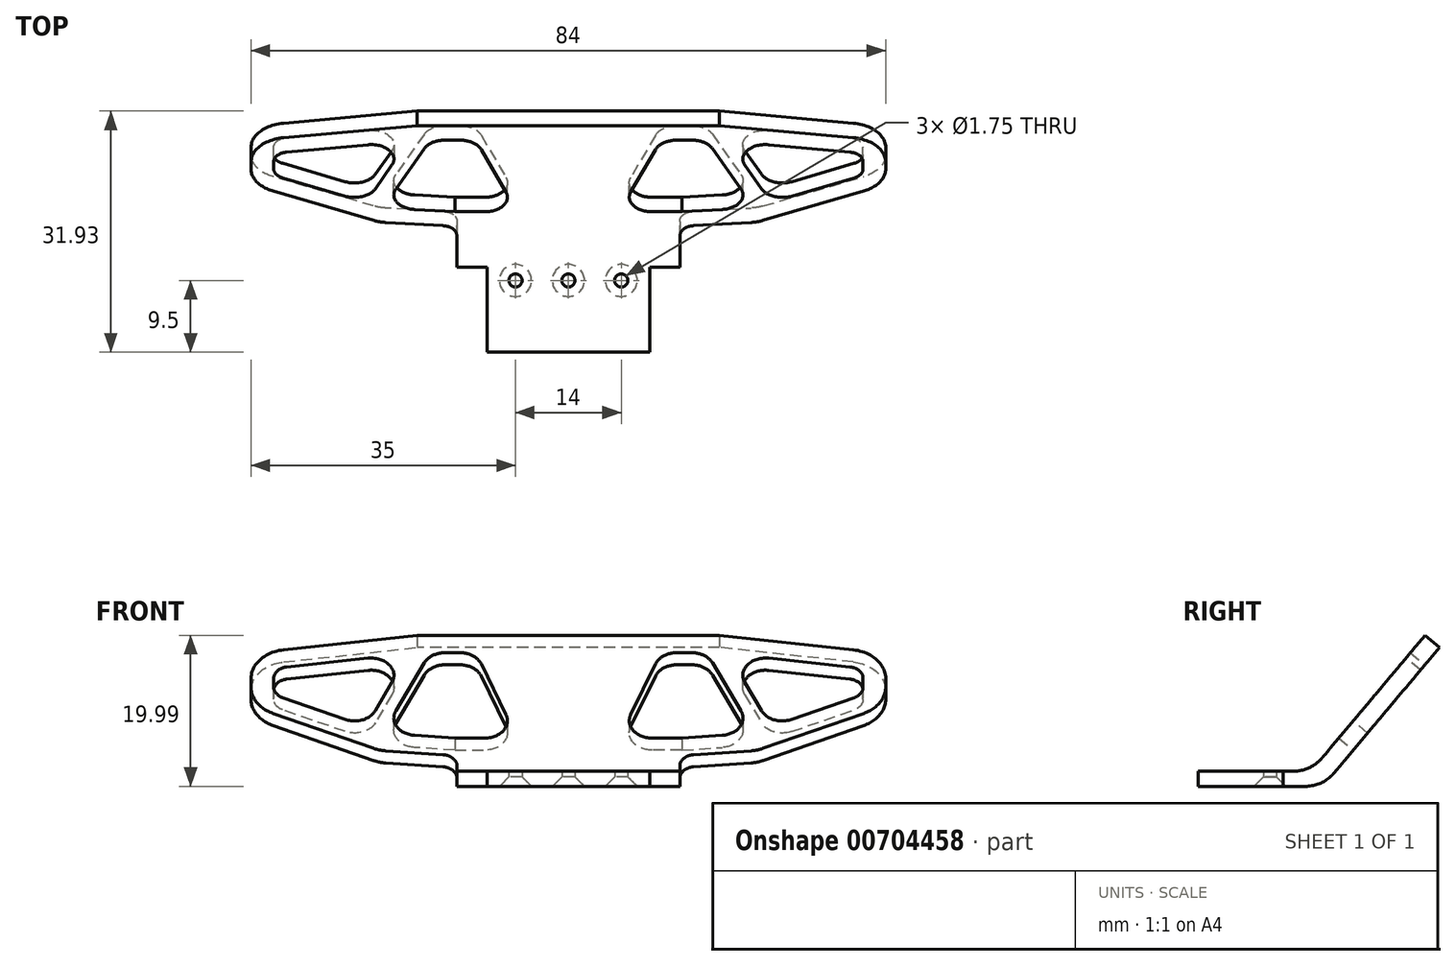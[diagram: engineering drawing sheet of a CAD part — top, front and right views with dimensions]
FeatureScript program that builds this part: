
annotation { "Feature Type Name" : "Feature", "Feature Type Description" : "" }
export const myFeature = defineFeature(function(context is Context, id is Id, definition is map)
    precondition{}
    {
        {
            var Q0;
            Q0=qCreatedBy(makeId("Top.planeOp"),FACE);
            var sketch = newSketch(context, id + "F0", { "sketchPlane" : qUnion([Q0])});
            skLineSegment(sketch, "E0", {"start": v(0, 0) * mm, "end": v(0, -25.33) * mm, "construction": true});
            skCircle(sketch, "E1", {"center": v(0, -7) * mm, "radius": 0.87 * mm});
            skCircle(sketch, "E2", {"center": v(-7, -7) * mm, "radius": 0.88 * mm});
            skLineSegment(sketch, "E3", {"start": v(0, 0) * mm, "end": v(-14.75, 0) * mm});
            skLineSegment(sketch, "E4", {"start": v(-10.75, -5.25) * mm, "end": v(-10.75, -16.5) * mm});
            skLineSegment(sketch, "E5", {"start": v(-10.75, -16.5) * mm, "end": v(0, -16.5) * mm});
            skLineSegment(sketch, "E6", {"start": v(-10.75, -5.25) * mm, "end": v(-14.75, -5.25) * mm});
            skLineSegment(sketch, "E7", {"start": v(-14.75, -5.25) * mm, "end": v(-14.75, 0) * mm});
            skLineSegment(sketch, "E8", {"start": v(-14.75, -2) * mm, "end": v(0, -2) * mm, "construction": true});
            skLineSegment(sketch, "E9.MirrorCS", {"start": v(0, 0) * mm, "end": v(14.75, 0) * mm});
            skLineSegment(sketch, "E10.MirrorCS", {"start": v(14.75, -5.25) * mm, "end": v(14.75, 0) * mm});
            skLineSegment(sketch, "E11.MirrorCS", {"start": v(10.75, -5.25) * mm, "end": v(14.75, -5.25) * mm});
            skLineSegment(sketch, "E12.MirrorCS", {"start": v(10.75, -5.25) * mm, "end": v(10.75, -16.5) * mm});
            skLineSegment(sketch, "E13.MirrorCS", {"start": v(10.75, -16.5) * mm, "end": v(0, -16.5) * mm});
            skCircle(sketch, "E14.MirrorC", {"center": v(7, -7) * mm, "radius": 0.88 * mm});
            skLineSegment(sketch, "E15", {"start": v(-14.75, 5) * mm, "end": v(14.75, 5) * mm, "construction": true});
            skSolve(sketch);
        }
        {
            var Q0;
            Q0=makeQuery(id+"F0.imprint","IMPRINT",FACE,{"disambiguationData":[TD([[makeQuery(id+"F0.imprint","IMPRINT",EDGE,{"derivedFrom":sQuery(id+"F0.wireOp",EDGE,"E1")}),-1.0]])]});
            extrude(context, id + "F1", {"entities" : qUnion([Q0]), "depth" : 2 * mm, "offsetDistance" : 25 * mm});
        }
        {
            var Q0;
            Q0=makeQuery(id+"F1.opExtrude","CAP_EDGE",EDGE,{"disambiguationData":[OSD([sQuery(id+"F0.wireOp",EDGE,"E3"),sQuery(id+"F0.wireOp",EDGE,"E9.MirrorCS")])],"isStart":true});
            cPlane(context, id + "F2", {"entities" : qUnion([Q0]), "cplaneType" : CPlaneType.LINE_ANGLE, "offset" : 25 * mm, "angle" : 40 * degree, "oppositeDirection" : true, "width" : 150 * mm, "height" : 150 * mm});
        }
        {
            var Q0;
            Q0=qCreatedBy(id+"F2.planeOp",FACE);
            var sketch = newSketch(context, id + "F3", { "sketchPlane" : qUnion([Q0])});
            skLineSegment(sketch, "E16.0", {"start": v(14.75, 0) * mm, "end": v(-14.75, 0) * mm});
            skLineSegment(sketch, "E17", {"start": v(0, 0) * mm, "end": v(0, 3.21) * mm, "construction": true});
            skLineSegment(sketch, "E18.0", {"start": v(14.75, 3.21) * mm, "end": v(-14.75, 3.21) * mm, "construction": true});
            skLineSegment(sketch, "E19", {"start": v(0, 24) * mm, "end": v(-20, 24) * mm});
            skLineSegment(sketch, "E20", {"start": v(-16.58, 3.37) * mm, "end": v(-24.15, 4.04) * mm});
            skLineSegment(sketch, "E21", {"start": v(-14.75, 0) * mm, "end": v(-14.75, 1.38) * mm});
            skPoint(sketch, "E22.visualSharp", {"position": v(-14.75, 3.21) * mm});
            skArc(sketch, "E22.filletArc", {"start": v(-14.75, 1.38) * mm, "mid": v(-15.28, 2.73) * mm, "end": v(-16.58, 3.37) * mm});
            skLineSegment(sketch, "E23", {"start": v(-25.78, 4.46) * mm, "end": v(-39.07, 10.5) * mm});
            skPoint(sketch, "E24.visualSharp", {"position": v(-25, 4.11) * mm});
            skArc(sketch, "E24.filletArc", {"start": v(-25.78, 4.46) * mm, "mid": v(-24.98, 4.18) * mm, "end": v(-24.15, 4.04) * mm});
            skLineSegment(sketch, "E25", {"start": v(-42, 15.05) * mm, "end": v(-42, 16.55) * mm});
            skLineSegment(sketch, "E26", {"start": v(-37.7, 21.5) * mm, "end": v(-20, 24) * mm});
            skPoint(sketch, "E27.visualSharp", {"position": v(-42, 20.9) * mm});
            skArc(sketch, "E27.filletArc", {"start": v(-37.7, 21.5) * mm, "mid": v(-40.77, 19.83) * mm, "end": v(-42, 16.55) * mm});
            skPoint(sketch, "E28.visualSharp", {"position": v(-42, 11.83) * mm});
            skArc(sketch, "E28.filletArc", {"start": v(-42, 15.05) * mm, "mid": v(-41.2, 12.34) * mm, "end": v(-39.07, 10.5) * mm});
            skLineSegment(sketch, "E29.MirrorCS", {"start": v(0, 24) * mm, "end": v(20, 24) * mm});
            skLineSegment(sketch, "E30.MirrorCS", {"start": v(37.7, 21.5) * mm, "end": v(20, 24) * mm});
            skArc(sketch, "E31.MirrorCS", {"start": v(37.7, 21.5) * mm, "mid": v(40.77, 19.83) * mm, "end": v(42, 16.55) * mm});
            skArc(sketch, "E32.MirrorCS", {"start": v(42, 15.05) * mm, "mid": v(41.2, 12.34) * mm, "end": v(39.07, 10.5) * mm});
            skLineSegment(sketch, "E33.MirrorCS", {"start": v(25.78, 4.46) * mm, "end": v(39.07, 10.5) * mm});
            skLineSegment(sketch, "E34.MirrorCS", {"start": v(16.58, 3.37) * mm, "end": v(24.15, 4.04) * mm});
            skArc(sketch, "E35.MirrorCS", {"start": v(14.75, 1.38) * mm, "mid": v(15.28, 2.73) * mm, "end": v(16.58, 3.37) * mm});
            skArc(sketch, "E36.MirrorCS", {"start": v(25.78, 4.46) * mm, "mid": v(24.98, 4.18) * mm, "end": v(24.15, 4.04) * mm});
            skLineSegment(sketch, "E37.MirrorCS", {"start": v(42, 15.05) * mm, "end": v(42, 16.55) * mm});
            skLineSegment(sketch, "E38", {"start": v(14.75, 1.38) * mm, "end": v(14.75, 0) * mm});
            skSolve(sketch);
        }
        {
            var Q0;
            Q0=makeQuery(id+"F3.imprint","IMPRINT",FACE,{"disambiguationData":[TD([[makeQuery(id+"F3.imprint","IMPRINT",EDGE,{"derivedFrom":sQuery(id+"F3.wireOp",EDGE,"E16.0")}),-1.0]])]});
            extrude(context, id + "F4", {"entities" : qUnion([Q0]), "operationType" : NewBodyOperationType.ADD, "oppositeDirection" : true, "depth" : 2.5 * mm, "offsetDistance" : 25 * mm});
        }
        {
            var Q0;
            Q0=makeQuery(id+"F4.opExtrude","CAP_FACE",FACE,{"disambiguationData":[OSD([sQuery(id+"F3.wireOp",EDGE,"E16.0"),sQuery(id+"F3.wireOp",EDGE,"E19"),sQuery(id+"F3.wireOp",EDGE,"E20"),sQuery(id+"F3.wireOp",EDGE,"E21"),sQuery(id+"F3.wireOp",EDGE,"E22.filletArc"),sQuery(id+"F3.wireOp",EDGE,"E23"),sQuery(id+"F3.wireOp",EDGE,"E24.filletArc"),sQuery(id+"F3.wireOp",EDGE,"E25"),sQuery(id+"F3.wireOp",EDGE,"E26"),sQuery(id+"F3.wireOp",EDGE,"E27.filletArc"),sQuery(id+"F3.wireOp",EDGE,"E28.filletArc"),sQuery(id+"F3.wireOp",EDGE,"E29.MirrorCS"),sQuery(id+"F3.wireOp",EDGE,"E30.MirrorCS"),sQuery(id+"F3.wireOp",EDGE,"E31.MirrorCS"),sQuery(id+"F3.wireOp",EDGE,"E32.MirrorCS"),sQuery(id+"F3.wireOp",EDGE,"E33.MirrorCS"),sQuery(id+"F3.wireOp",EDGE,"E34.MirrorCS"),sQuery(id+"F3.wireOp",EDGE,"E35.MirrorCS"),sQuery(id+"F3.wireOp",EDGE,"E36.MirrorCS"),sQuery(id+"F3.wireOp",EDGE,"E37.MirrorCS"),sQuery(id+"F3.wireOp",EDGE,"E38")])],"isStart":true});
            var sketch = newSketch(context, id + "F5", { "sketchPlane" : qUnion([Q0])});
            skLineSegment(sketch, "E39.0", {"start": v(-18.27, 21) * mm, "end": v(-12.27, 21) * mm});
            skLineSegment(sketch, "E39.1", {"start": v(-37.28, 18.53) * mm, "end": v(-21.1, 20.81) * mm});
            skArc(sketch, "E39.2", {"start": v(-37.28, 18.53) * mm, "mid": v(-38.5, 17.86) * mm, "end": v(-39, 16.55) * mm});
            skLineSegment(sketch, "E39.3", {"start": v(-39, 15.05) * mm, "end": v(-39, 16.55) * mm});
            skLineSegment(sketch, "E39.4", {"start": v(-15.03, 6.25) * mm, "end": v(-23.89, 7.02) * mm});
            skArc(sketch, "E39.5", {"start": v(-24.54, 7.2) * mm, "mid": v(-24.22, 7.08) * mm, "end": v(-23.89, 7.02) * mm});
            skLineSegment(sketch, "E39.6", {"start": v(-26.81, 8.23) * mm, "end": v(-37.83, 13.23) * mm});
            skArc(sketch, "E39.7", {"start": v(-39, 15.05) * mm, "mid": v(-38.68, 13.97) * mm, "end": v(-37.83, 13.23) * mm});
            skLineSegment(sketch, "E40", {"start": v(-21.1, 20.81) * mm, "end": v(-26.81, 8.23) * mm});
            skLineSegment(sketch, "E41.0", {"start": v(-18.27, 21) * mm, "end": v(-24.54, 7.2) * mm});
            skLineSegment(sketch, "E42", {"start": v(-15.03, 6.25) * mm, "end": v(-6.73, 6.25) * mm});
            skLineSegment(sketch, "E43", {"start": v(-12.27, 21) * mm, "end": v(-6.73, 6.25) * mm});
            skLineSegment(sketch, "E44.MirrorCS", {"start": v(12.27, 21) * mm, "end": v(6.73, 6.25) * mm});
            skLineSegment(sketch, "E45.MirrorCS", {"start": v(18.27, 21) * mm, "end": v(24.54, 7.2) * mm});
            skArc(sketch, "E46.MirrorCS", {"start": v(24.54, 7.2) * mm, "mid": v(24.22, 7.08) * mm, "end": v(23.89, 7.02) * mm});
            skLineSegment(sketch, "E47.MirrorCS", {"start": v(15.03, 6.25) * mm, "end": v(23.89, 7.02) * mm});
            skLineSegment(sketch, "E48.MirrorCS", {"start": v(15.03, 6.25) * mm, "end": v(6.73, 6.25) * mm});
            skLineSegment(sketch, "E49.MirrorCS", {"start": v(21.1, 20.81) * mm, "end": v(26.81, 8.23) * mm});
            skLineSegment(sketch, "E50.MirrorCS", {"start": v(37.28, 18.53) * mm, "end": v(21.1, 20.81) * mm});
            skLineSegment(sketch, "E51.MirrorCS", {"start": v(26.81, 8.23) * mm, "end": v(37.83, 13.23) * mm});
            skArc(sketch, "E52.MirrorCS", {"start": v(39, 15.05) * mm, "mid": v(38.68, 13.97) * mm, "end": v(37.83, 13.23) * mm});
            skLineSegment(sketch, "E53.MirrorCS", {"start": v(39, 15.05) * mm, "end": v(39, 16.55) * mm});
            skArc(sketch, "E54.MirrorCS", {"start": v(37.28, 18.53) * mm, "mid": v(38.5, 17.86) * mm, "end": v(39, 16.55) * mm});
            skLineSegment(sketch, "E55.trimOffspring", {"start": v(12.27, 21) * mm, "end": v(18.27, 21) * mm});
            skPoint(sketch, "E56.orphan", {"position": v(0, 6.25) * mm});
            skSolve(sketch);
        }
        {
            var Q0;
            Q0=makeQuery(id+"F5.imprint","IMPRINT",FACE,{"disambiguationData":[TD([[makeQuery(id+"F5.imprint","IMPRINT",EDGE,{"derivedFrom":sQuery(id+"F5.wireOp",EDGE,"E39.1")}),-1.0]])]});
            var Q1;
            Q1=makeQuery(id+"F5.imprint","IMPRINT",FACE,{"disambiguationData":[TD([[makeQuery(id+"F5.imprint","IMPRINT",EDGE,{"derivedFrom":sQuery(id+"F5.wireOp",EDGE,"E39.0")}),-1.0]])]});
            var Q2;
            Q2=makeQuery(id+"F5.imprint","IMPRINT",FACE,{"disambiguationData":[TD([[makeQuery(id+"F5.imprint","IMPRINT",EDGE,{"derivedFrom":sQuery(id+"F5.wireOp",EDGE,"E44.MirrorCS")}),1.0]])]});
            var Q3;
            Q3=makeQuery(id+"F5.imprint","IMPRINT",FACE,{"disambiguationData":[TD([[makeQuery(id+"F5.imprint","IMPRINT",EDGE,{"derivedFrom":sQuery(id+"F5.wireOp",EDGE,"E49.MirrorCS")}),1.0]])]});
            extrude(context, id + "F6", {"entities" : qUnion([Q0, Q1, Q2, Q3]), "operationType" : NewBodyOperationType.REMOVE, "endBound" : BoundingType.THROUGH_ALL, "oppositeDirection" : true, "depth" : 25 * mm, "offsetDistance" : 25 * mm});
        }
        {
            var Q0;
            Q0=makeQuery(id+"F4.boolean.opBoolean","INTERSECT",EDGE,{"derivedFrom":[makeQuery(id+"F1.opExtrude","CAP_FACE",FACE,{"disambiguationData":[OSD([sQuery(id+"F0.wireOp",EDGE,"E1"),sQuery(id+"F0.wireOp",EDGE,"E2"),sQuery(id+"F0.wireOp",EDGE,"E3"),sQuery(id+"F0.wireOp",EDGE,"E4"),sQuery(id+"F0.wireOp",EDGE,"E5"),sQuery(id+"F0.wireOp",EDGE,"E6"),sQuery(id+"F0.wireOp",EDGE,"E7"),sQuery(id+"F0.wireOp",EDGE,"E9.MirrorCS"),sQuery(id+"F0.wireOp",EDGE,"E10.MirrorCS"),sQuery(id+"F0.wireOp",EDGE,"E11.MirrorCS"),sQuery(id+"F0.wireOp",EDGE,"E12.MirrorCS"),sQuery(id+"F0.wireOp",EDGE,"E13.MirrorCS"),sQuery(id+"F0.wireOp",EDGE,"E14.MirrorC")])],"isStart":false}),makeQuery(id+"F4.opExtrude","CAP_FACE",FACE,{"disambiguationData":[OSD([sQuery(id+"F3.wireOp",EDGE,"E16.0"),sQuery(id+"F3.wireOp",EDGE,"E19"),sQuery(id+"F3.wireOp",EDGE,"E20"),sQuery(id+"F3.wireOp",EDGE,"E21"),sQuery(id+"F3.wireOp",EDGE,"E22.filletArc"),sQuery(id+"F3.wireOp",EDGE,"E23"),sQuery(id+"F3.wireOp",EDGE,"E24.filletArc"),sQuery(id+"F3.wireOp",EDGE,"E25"),sQuery(id+"F3.wireOp",EDGE,"E26"),sQuery(id+"F3.wireOp",EDGE,"E27.filletArc"),sQuery(id+"F3.wireOp",EDGE,"E28.filletArc"),sQuery(id+"F3.wireOp",EDGE,"E29.MirrorCS"),sQuery(id+"F3.wireOp",EDGE,"E30.MirrorCS"),sQuery(id+"F3.wireOp",EDGE,"E31.MirrorCS"),sQuery(id+"F3.wireOp",EDGE,"E32.MirrorCS"),sQuery(id+"F3.wireOp",EDGE,"E33.MirrorCS"),sQuery(id+"F3.wireOp",EDGE,"E34.MirrorCS"),sQuery(id+"F3.wireOp",EDGE,"E35.MirrorCS"),sQuery(id+"F3.wireOp",EDGE,"E36.MirrorCS"),sQuery(id+"F3.wireOp",EDGE,"E37.MirrorCS"),sQuery(id+"F3.wireOp",EDGE,"E38")])],"isStart":false})]});
            var Q1;
            Q1=makeQuery(id+"F4.boolean.opBoolean","MERGE",EDGE,{"derivedFrom":[makeQuery(id+"F1.opExtrude","CAP_EDGE",EDGE,{"disambiguationData":[OSD([sQuery(id+"F0.wireOp",EDGE,"E3"),sQuery(id+"F0.wireOp",EDGE,"E9.MirrorCS")])],"isStart":true}),makeQuery(id+"F4.opExtrude","CAP_EDGE",EDGE,{"disambiguationData":[OSD([sQuery(id+"F3.wireOp",EDGE,"E16.0")])],"isStart":true})]});
            fillet(context, id + "F7", {"entities" : qUnion([Q0, Q1]), "tangentPropagation" : true, "radius" : 5 * mm, "defaultsChanged" : false, "vertexSettings" : [], "allowEdgeOverflow" : false});
        }
        {
            var Q0;
            Q0=makeQuery(id+"F6.boolean.opBoolean","COPY",EDGE,{"derivedFrom":makeQuery(id+"F6.opExtrude","SWEPT_EDGE",EDGE,{"disambiguationData":[OSD([sQuery(id+"F5.wireOp",EDGE,"E49.MirrorCS"),sQuery(id+"F5.wireOp",EDGE,"E50.MirrorCS")])]})});
            var Q1;
            Q1=makeQuery(id+"F6.boolean.opBoolean","COPY",EDGE,{"derivedFrom":makeQuery(id+"F6.opExtrude","SWEPT_EDGE",EDGE,{"disambiguationData":[OSD([sQuery(id+"F5.wireOp",EDGE,"E49.MirrorCS"),sQuery(id+"F5.wireOp",EDGE,"E51.MirrorCS")])]})});
            var Q2;
            Q2=makeQuery(id+"F6.boolean.opBoolean","COPY",EDGE,{"derivedFrom":makeQuery(id+"F6.opExtrude","SWEPT_EDGE",EDGE,{"disambiguationData":[OSD([sQuery(id+"F5.wireOp",EDGE,"E45.MirrorCS"),sQuery(id+"F5.wireOp",EDGE,"E46.MirrorCS")])]})});
            var Q3;
            Q3=makeQuery(id+"F6.boolean.opBoolean","COPY",EDGE,{"derivedFrom":makeQuery(id+"F6.opExtrude","SWEPT_EDGE",EDGE,{"disambiguationData":[OSD([sQuery(id+"F5.wireOp",EDGE,"E44.MirrorCS"),sQuery(id+"F5.wireOp",EDGE,"E48.MirrorCS")])]})});
            var Q4;
            Q4=makeQuery(id+"F6.boolean.opBoolean","COPY",EDGE,{"derivedFrom":makeQuery(id+"F6.opExtrude","SWEPT_EDGE",EDGE,{"disambiguationData":[OSD([sQuery(id+"F5.wireOp",EDGE,"E44.MirrorCS"),sQuery(id+"F5.wireOp",EDGE,"E55.trimOffspring")])]})});
            var Q5;
            Q5=makeQuery(id+"F6.boolean.opBoolean","COPY",EDGE,{"derivedFrom":makeQuery(id+"F6.opExtrude","SWEPT_EDGE",EDGE,{"disambiguationData":[OSD([sQuery(id+"F5.wireOp",EDGE,"E45.MirrorCS"),sQuery(id+"F5.wireOp",EDGE,"E55.trimOffspring")])]})});
            var Q6;
            Q6=makeQuery(id+"F6.boolean.opBoolean","COPY",EDGE,{"derivedFrom":makeQuery(id+"F6.opExtrude","SWEPT_EDGE",EDGE,{"disambiguationData":[OSD([sQuery(id+"F5.wireOp",EDGE,"E39.0"),sQuery(id+"F5.wireOp",EDGE,"E43")])]})});
            var Q7;
            Q7=makeQuery(id+"F6.boolean.opBoolean","COPY",EDGE,{"derivedFrom":makeQuery(id+"F6.opExtrude","SWEPT_EDGE",EDGE,{"disambiguationData":[OSD([sQuery(id+"F5.wireOp",EDGE,"E39.0"),sQuery(id+"F5.wireOp",EDGE,"E41.0")])]})});
            var Q8;
            Q8=makeQuery(id+"F6.boolean.opBoolean","COPY",EDGE,{"derivedFrom":makeQuery(id+"F6.opExtrude","SWEPT_EDGE",EDGE,{"disambiguationData":[OSD([sQuery(id+"F5.wireOp",EDGE,"E39.5"),sQuery(id+"F5.wireOp",EDGE,"E41.0")])]})});
            var Q9;
            Q9=makeQuery(id+"F6.boolean.opBoolean","COPY",EDGE,{"derivedFrom":makeQuery(id+"F6.opExtrude","SWEPT_EDGE",EDGE,{"disambiguationData":[OSD([sQuery(id+"F5.wireOp",EDGE,"E42"),sQuery(id+"F5.wireOp",EDGE,"E43")])]})});
            var Q10;
            Q10=makeQuery(id+"F6.boolean.opBoolean","COPY",EDGE,{"derivedFrom":makeQuery(id+"F6.opExtrude","SWEPT_EDGE",EDGE,{"disambiguationData":[OSD([sQuery(id+"F5.wireOp",EDGE,"E39.6"),sQuery(id+"F5.wireOp",EDGE,"E40")])]})});
            var Q11;
            Q11=makeQuery(id+"F6.boolean.opBoolean","COPY",EDGE,{"derivedFrom":makeQuery(id+"F6.opExtrude","SWEPT_EDGE",EDGE,{"disambiguationData":[OSD([sQuery(id+"F5.wireOp",EDGE,"E39.1"),sQuery(id+"F5.wireOp",EDGE,"E40")])]})});
            fillet(context, id + "F8", {"entities" : qUnion([Q0, Q1, Q2, Q3, Q4, Q5, Q6, Q7, Q8, Q9, Q10, Q11]), "tangentPropagation" : true, "radius" : 3 * mm, "defaultsChanged" : true, "vertexSettings" : [], "allowEdgeOverflow" : false});
        }
        {
            var Q0;
            Q0=makeQuery(id+"F1.opExtrude","CAP_EDGE",EDGE,{"disambiguationData":[OSD([sQuery(id+"F0.wireOp",EDGE,"E2")])],"isStart":true});
            var Q1;
            Q1=makeQuery(id+"F1.opExtrude","CAP_EDGE",EDGE,{"disambiguationData":[OSD([sQuery(id+"F0.wireOp",EDGE,"E1")])],"isStart":true});
            var Q2;
            Q2=makeQuery(id+"F1.opExtrude","CAP_EDGE",EDGE,{"disambiguationData":[OSD([sQuery(id+"F0.wireOp",EDGE,"E14.MirrorC")])],"isStart":true});
            chamfer(context, id + "F9", {"entities" : qUnion([Q0, Q1, Q2]), "width" : 1.25 * mm, "tangentPropagation" : true});
        }
    });
